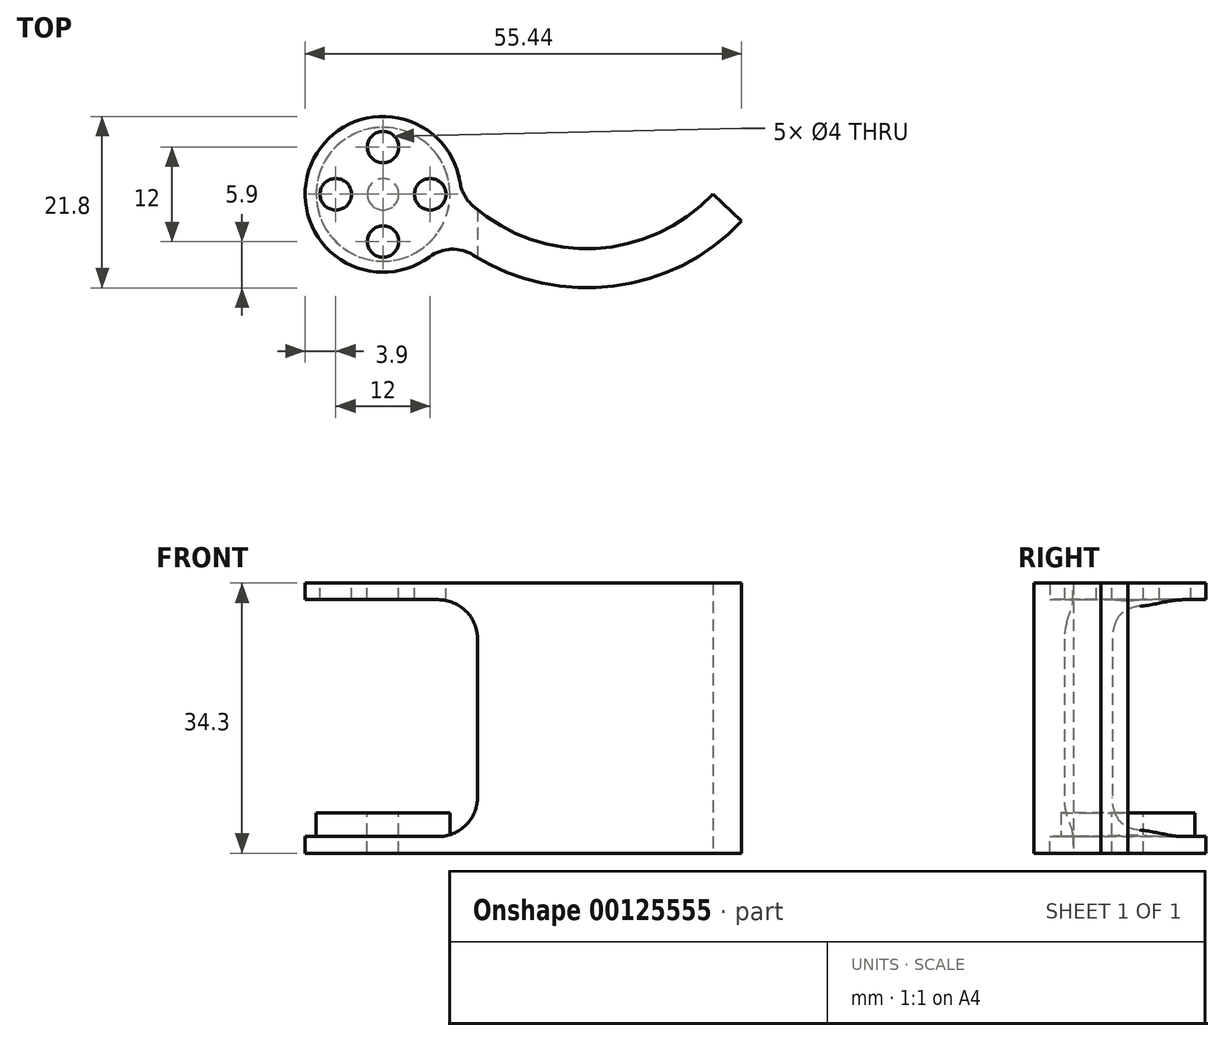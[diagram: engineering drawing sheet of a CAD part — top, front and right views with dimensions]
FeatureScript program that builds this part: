
annotation { "Feature Type Name" : "Feature", "Feature Type Description" : "" }
export const myFeature = defineFeature(function(context is Context, id is Id, definition is map)
    precondition{}
    {
        {
            var Q0;
            Q0=qCreatedBy(makeId("Top.planeOp"),FACE);
            var sketch = newSketch(context, id + "F0", { "sketchPlane" : qUnion([Q0])});
            skArc(sketch, "E0", {"start": v(9.9, 0) * mm, "mid": v(-9.5, 2.8) * mm, "end": v(8.3, -5.38) * mm});
            skArc(sketch, "E1", {"start": v(9.9, 0) * mm, "mid": v(25.9, -6.9) * mm, "end": v(41.9, 0) * mm});
            skArc(sketch, "E2", {"start": v(8.3, -5.38) * mm, "mid": v(27.31, -11.86) * mm, "end": v(45.54, -3.43) * mm});
            skLineSegment(sketch, "E3", {"start": v(41.9, 0) * mm, "end": v(45.54, -3.43) * mm});
            skSolve(sketch);
        }
        {
            var Q0;
            Q0 = qSketchRegion(id + "F0", true);
            extrude(context, id + "F1", {"entities" : qUnion([Q0]), "depth" : 17.15 * mm});
        }
        {
            var Q0;
            Q0=qCreatedBy(makeId("Front.planeOp"),FACE);
            var sketch = newSketch(context, id + "F2", { "sketchPlane" : qUnion([Q0])});
            skLineSegment(sketch, "E4.bottom", {"start": v(-20, 15.05) * mm, "end": v(7, 15.05) * mm});
            skLineSegment(sketch, "E4.top", {"start": v(-20, 0) * mm, "end": v(12, 0) * mm});
            skLineSegment(sketch, "E4.left", {"start": v(-20, 15.05) * mm, "end": v(-20, 0) * mm});
            skLineSegment(sketch, "E4.right", {"start": v(12, 10.05) * mm, "end": v(12, 0) * mm});
            skPoint(sketch, "E5.visualSharp", {"position": v(12, 15.05) * mm});
            skArc(sketch, "E5.filletArc", {"start": v(12, 10.05) * mm, "mid": v(10.54, 13.59) * mm, "end": v(7, 15.05) * mm});
            skSolve(sketch);
        }
        {
            var Q0;
            Q0 = qSketchRegion(id + "F2", true);
            extrude(context, id + "F3", {"entities" : qUnion([Q0]), "operationType" : NewBodyOperationType.REMOVE, "endBound" : BoundingType.THROUGH_ALL, "oppositeDirection" : true, "depth" : 25 * mm, "hasSecondDirection" : true, "secondDirectionBound" : BoundingType.THROUGH_ALL, "secondDirectionOppositeDirection" : false, "secondDirectionDepth" : 25 * mm});
        }
        {
            var Q0;
            Q0=makeQuery(id+"F1.opExtrude","SWEPT_BODY",BODY,{"disambiguationData":[OSD([sQuery(id+"F0.wireOp",EDGE,"E0"),sQuery(id+"F0.wireOp",EDGE,"E1"),sQuery(id+"F0.wireOp",EDGE,"E2"),sQuery(id+"F0.wireOp",EDGE,"E3")])]});
            var Q1;
            Q1=qCreatedBy(makeId("Top.planeOp"),FACE);
            mirror(context, id + "F4", {"operationType" : NewBodyOperationType.ADD, "entities" : qUnion([Q0]), "mirrorPlane" : qUnion([Q1])});
        }
        {
            var Q0;
            Q0=makeQuery(id+"F4.opPattern","COPY",FACE,{"derivedFrom":makeQuery(id+"F3.boolean.opBoolean","COPY",FACE,{"derivedFrom":makeQuery(id+"F3.opExtrude","SWEPT_FACE",FACE,{"disambiguationData":[OSD([sQuery(id+"F2.wireOp",EDGE,"E4.bottom")])]})}),"instanceName":"1"});
            var sketch = newSketch(context, id + "F5", { "sketchPlane" : qUnion([Q0])});
            skCircle(sketch, "E6", {"center": v(0, 0) * mm, "radius": 8.5 * mm});
            skSolve(sketch);
        }
        {
            var Q0;
            Q0 = qSketchRegion(id + "F5", true);
            extrude(context, id + "F6", {"entities" : qUnion([Q0]), "operationType" : NewBodyOperationType.ADD, "depth" : 3 * mm});
        }
        {
            var Q0;
            Q0=makeQuery(id+"F6.opExtrude","CAP_FACE",FACE,{"disambiguationData":[OSD([sQuery(id+"F5.wireOp",EDGE,"E6")])],"isStart":false});
            var sketch = newSketch(context, id + "F7", { "sketchPlane" : qUnion([Q0])});
            skCircle(sketch, "E7", {"center": v(0, 0) * mm, "radius": 2 * mm});
            skSolve(sketch);
        }
        {
            var Q0;
            Q0 = qSketchRegion(id + "F7", true);
            extrude(context, id + "F8", {"entities" : qUnion([Q0]), "operationType" : NewBodyOperationType.REMOVE, "endBound" : BoundingType.THROUGH_ALL, "oppositeDirection" : true, "depth" : 25 * mm});
        }
        {
            var Q0;
            Q0=makeQuery(id+"F1.opExtrude","CAP_FACE",FACE,{"disambiguationData":[OSD([sQuery(id+"F0.wireOp",EDGE,"E0"),sQuery(id+"F0.wireOp",EDGE,"E1"),sQuery(id+"F0.wireOp",EDGE,"E2"),sQuery(id+"F0.wireOp",EDGE,"E3")])],"isStart":false});
            var sketch = newSketch(context, id + "F9", { "sketchPlane" : qUnion([Q0])});
            skCircle(sketch, "E8", {"center": v(6, 0) * mm, "radius": 2 * mm});
            skCircle(sketch, "E9", {"center": v(0, 0) * mm, "radius": 6 * mm, "construction": true});
            skCircle(sketch, "E10", {"center": v(0, -6) * mm, "radius": 2 * mm});
            skCircle(sketch, "E11", {"center": v(-6, 0) * mm, "radius": 2 * mm});
            skCircle(sketch, "E12", {"center": v(0, 6) * mm, "radius": 2 * mm});
            skSolve(sketch);
        }
        {
            var Q0;
            Q0 = qSketchRegion(id + "F9", true);
            var Q1;
            Q1=qCreatedBy(makeId("Top.planeOp"),FACE);
            extrude(context, id + "F10", {"entities" : qUnion([Q0]), "operationType" : NewBodyOperationType.REMOVE, "endBound" : BoundingType.UP_TO_SURFACE, "oppositeDirection" : true, "endBoundEntityFace" : qUnion([Q1]), "depth" : 25 * mm});
        }
        {
            var Q0;
            Q0=makeQuery(id+"F4.opPattern","COPY",EDGE,{"derivedFrom":makeQuery(id+"F1.opExtrude","SWEPT_EDGE",EDGE,{"disambiguationData":[OSD([sQuery(id+"F0.wireOp",EDGE,"E0"),sQuery(id+"F0.wireOp",EDGE,"E2")])]}),"instanceName":"1"});
            var Q1;
            Q1=makeQuery(id+"F1.opExtrude","SWEPT_EDGE",EDGE,{"disambiguationData":[OSD([sQuery(id+"F0.wireOp",EDGE,"E0"),sQuery(id+"F0.wireOp",EDGE,"E2")])]});
            var Q2;
            Q2=makeQuery(id+"F4.opPattern","COPY",EDGE,{"derivedFrom":makeQuery(id+"F1.opExtrude","SWEPT_EDGE",EDGE,{"disambiguationData":[OSD([sQuery(id+"F0.wireOp",EDGE,"E0"),sQuery(id+"F0.wireOp",EDGE,"E1")])]}),"instanceName":"1"});
            var Q3;
            Q3=makeQuery(id+"F1.opExtrude","SWEPT_EDGE",EDGE,{"disambiguationData":[OSD([sQuery(id+"F0.wireOp",EDGE,"E0"),sQuery(id+"F0.wireOp",EDGE,"E1")])]});
            fillet(context, id + "F11", {"entities" : qUnion([Q0, Q1, Q2, Q3]), "radius" : 5 * mm, "tangentPropagation" : true, "allowEdgeOverflow" : false});
        }
    });
